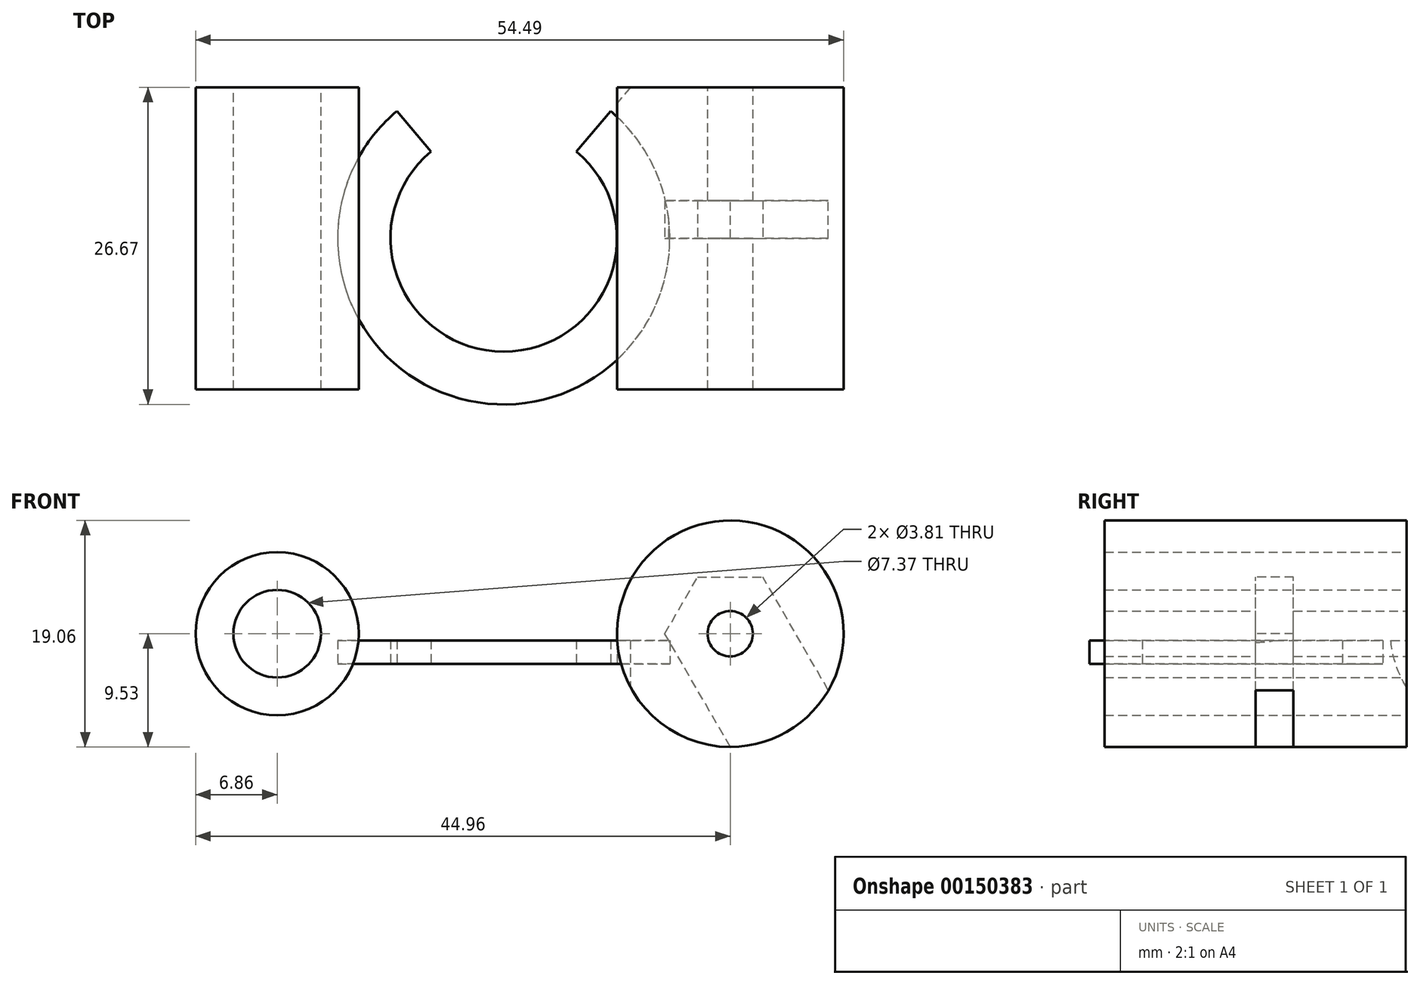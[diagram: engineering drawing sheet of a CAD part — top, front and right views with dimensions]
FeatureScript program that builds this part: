
annotation { "Feature Type Name" : "Feature", "Feature Type Description" : "" }
export const myFeature = defineFeature(function(context is Context, id is Id, definition is map)
    precondition{}
    {
        {
            var Q0;
            Q0=qCreatedBy(makeId("Front.planeOp"),FACE);
            var sketch = newSketch(context, id + "F0", { "sketchPlane" : qUnion([Q0])});
            skCircle(sketch, "E0", {"center": v(-19.05, 2.54) * mm, "radius": 3.68 * mm});
            skCircle(sketch, "E1", {"center": v(-19.05, 2.54) * mm, "radius": 6.86 * mm});
            skCircle(sketch, "E2", {"center": v(19.05, 2.54) * mm, "radius": 1.9 * mm});
            skLineSegment(sketch, "E3", {"start": v(-19.05, 2.54) * mm, "end": v(19.05, 2.54) * mm, "construction": true});
            skLineSegment(sketch, "E4", {"start": v(0, 2.54) * mm, "end": v(0, 0) * mm, "construction": true});
            skCircle(sketch, "E5", {"center": v(19.05, 2.54) * mm, "radius": 9.53 * mm});
            skSolve(sketch);
        }
        {
            var Q0;
            Q0 = qSketchRegion(id + "F0", true);
            extrude(context, id + "F1", {"entities" : qUnion([Q0]), "endBound" : BoundingType.SYMMETRIC, "depth" : 25.4 * mm});
        }
        {
            var Q0;
            Q0=qCreatedBy(makeId("Top.planeOp"),FACE);
            var sketch = newSketch(context, id + "F2", { "sketchPlane" : qUnion([Q0])});
            skCircle(sketch, "E6", {"center": v(0, 0) * mm, "radius": 9.53 * mm});
            skCircle(sketch, "E7", {"center": v(0, 0) * mm, "radius": 13.97 * mm});
            skSolve(sketch);
        }
        {
            var Q0;
            Q0 = qSketchRegion(id + "F2", true);
            extrude(context, id + "F3", {"entities" : qUnion([Q0]), "depth" : 1.98 * mm});
        }
        {
            var Q0;
            Q0=makeQuery(id+"F3.opExtrude","CAP_FACE",FACE,{"disambiguationData":[OSD([sQuery(id+"F2.wireOp",EDGE,"E6"),sQuery(id+"F2.wireOp",EDGE,"E7")])],"isStart":false});
            var sketch = newSketch(context, id + "F4", { "sketchPlane" : qUnion([Q0])});
            skLineSegment(sketch, "E8", {"start": v(0, 0) * mm, "end": v(-15.07, 17.96) * mm});
            skLineSegment(sketch, "E9", {"start": v(-15.07, 17.96) * mm, "end": v(15.07, 17.96) * mm});
            skLineSegment(sketch, "E10", {"start": v(15.07, 17.96) * mm, "end": v(0, 0) * mm});
            skLineSegment(sketch, "E11", {"start": v(0, 17.96) * mm, "end": v(0, 0) * mm, "construction": true});
            skSolve(sketch);
        }
        {
            var Q0;
            Q0 = qSketchRegion(id + "F4", true);
            extrude(context, id + "F5", {"entities" : qUnion([Q0]), "operationType" : NewBodyOperationType.REMOVE, "oppositeDirection" : true, "depth" : 25.4 * mm});
        }
        {
            var Q0;
            Q0=qCreatedBy(makeId("Front.planeOp"),FACE);
            var sketch = newSketch(context, id + "F6", { "sketchPlane" : qUnion([Q0])});
            skCircle(sketch, "E12.cCircle", {"center": v(19.05, 2.54) * mm, "radius": 4.76 * mm, "construction": true});
            skLineSegment(sketch, "E12.0", {"start": v(16.3, 7.3) * mm, "end": v(21.8, 7.3) * mm});
            skLineSegment(sketch, "E12.1", {"start": v(21.8, 7.3) * mm, "end": v(24.55, 2.54) * mm});
            skLineSegment(sketch, "E12.4", {"start": v(16.3, -2.22) * mm, "end": v(13.55, 2.54) * mm});
            skLineSegment(sketch, "E12.5", {"start": v(13.55, 2.54) * mm, "end": v(16.3, 7.3) * mm});
            skPoint(sketch, "E12.0.midPoint", {"position": v(19.05, 7.3) * mm});
            skLineSegment(sketch, "E13", {"start": v(16.3, -2.22) * mm, "end": v(23.06, -13.93) * mm});
            skLineSegment(sketch, "E14", {"start": v(23.06, -13.93) * mm, "end": v(31.7, -9.84) * mm});
            skLineSegment(sketch, "E15", {"start": v(31.7, -9.84) * mm, "end": v(24.55, 2.54) * mm});
            skPoint(sketch, "E16.orphan", {"position": v(21.8, -2.22) * mm});
            skSolve(sketch);
        }
        {
            var Q0;
            Q0 = qSketchRegion(id + "F6", true);
            extrude(context, id + "F7", {"entities" : qUnion([Q0]), "operationType" : NewBodyOperationType.REMOVE, "oppositeDirection" : true, "depth" : 3.17 * mm});
        }
    });
